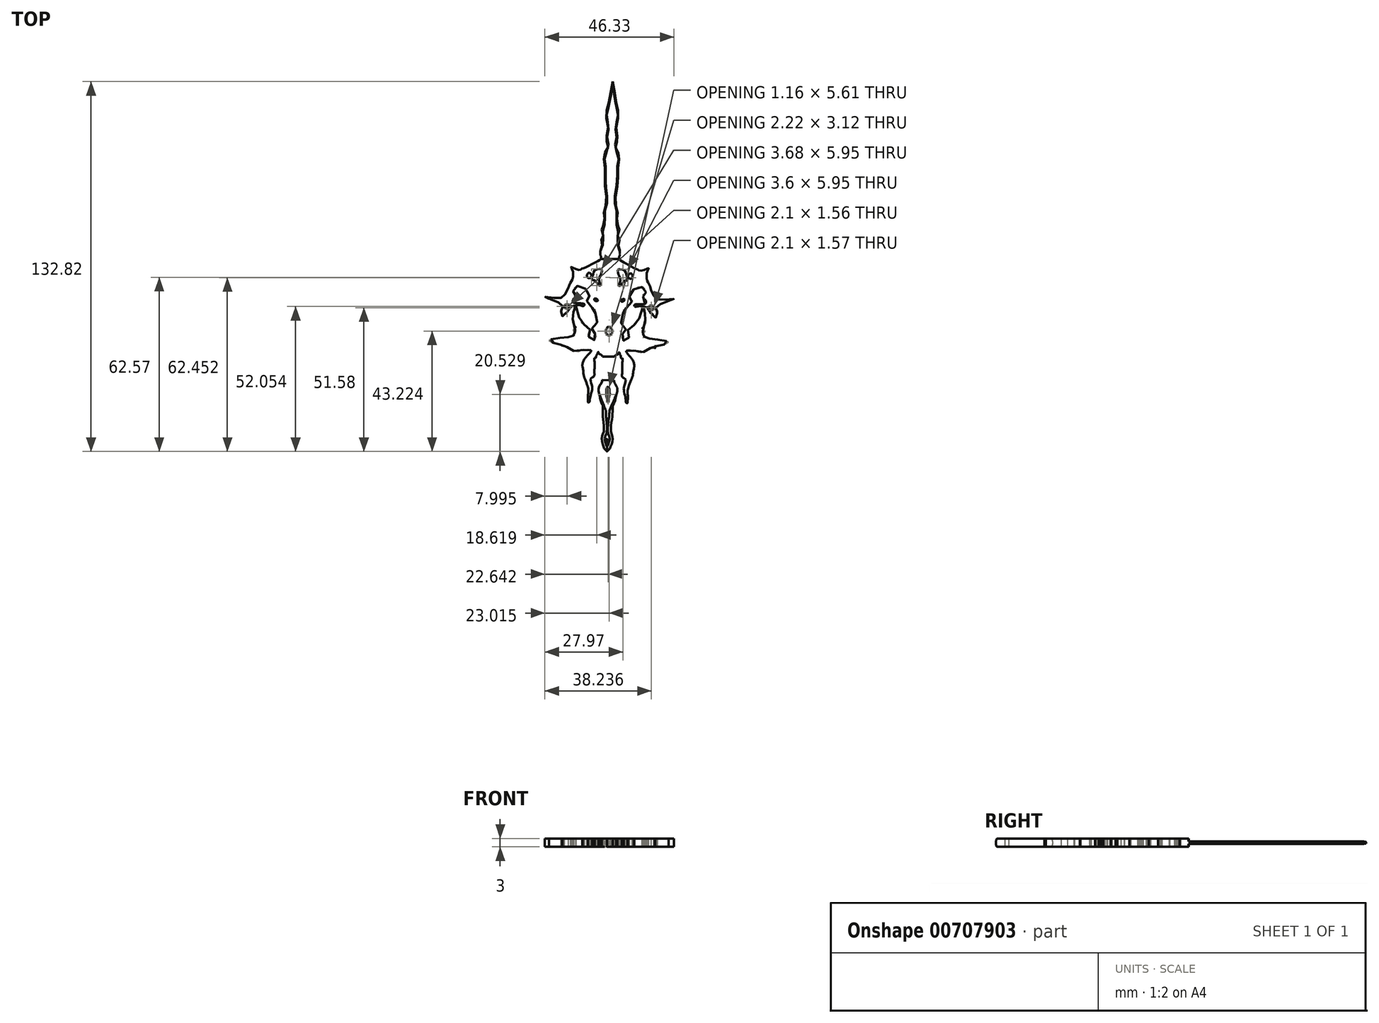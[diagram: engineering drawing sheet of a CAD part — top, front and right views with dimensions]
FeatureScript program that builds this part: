
annotation { "Feature Type Name" : "Feature", "Feature Type Description" : "" }
export const myFeature = defineFeature(function(context is Context, id is Id, definition is map)
    precondition{}
    {
        {
            var Q0;
            Q0=qCreatedBy(makeId("Top.planeOp"),FACE);
            var sketch = newSketch(context, id + "F0", { "sketchPlane" : qUnion([Q0])});
            skFitSpline(sketch, "E0", {"points": [v(17.67, 61.71) * mm, v(18.65, 55.7) * mm, v(19.3, 52.2) * mm, v(19.7, 49.3) * mm, v(18.9, 45.25) * mm, v(19.3, 41.85) * mm, v(19.22, 40.23) * mm, v(18.65, 38.77) * mm, v(19.14, 36.83) * mm, v(20.03, 35.45) * mm, v(19.7, 32.38) * mm, v(19.46, 28.25) * mm, v(19.3, 24.28) * mm, v(18.57, 19.18) * mm, v(19.14, 15.86) * mm, v(19.46, 13.6) * mm, v(19.06, 11.9) * mm, v(19.7, 9.47) * mm, v(20.1, 8.82) * mm, v(19.7, 7.77) * mm, v(19.54, 5.74) * mm, v(20.03, 4.85) * mm, v(19.79, 3.56) * mm, v(19.62, 2.42) * mm, v(20.2, 1.2) * mm], "startDerivative": vector(15.69, -96.68) * mm, "endDerivative": vector(24.07, -39.42) * mm});
            skFitSpline(sketch, "E1", {"points": [v(20.2, 1.2) * mm, v(20.2, 0.5) * mm, v(20.2, -0.63) * mm, v(19.94, -1.16) * mm, v(19.94, -2.05) * mm, v(20.7, -2.66) * mm, v(21.76, -3.3) * mm, v(23.21, -4.03) * mm, v(25.12, -5.2) * mm, v(26.5, -5.73) * mm, v(26.94, -6.06) * mm, v(28.64, -6.1) * mm, v(30.5, -5.29) * mm, v(29.93, -6.58) * mm, v(29.77, -8.24) * mm, v(29.97, -9.94) * mm, v(30.7, -11.03) * mm, v(31.3, -12.98) * mm], "startDerivative": vector(-0.52, -14.7) * mm, "endDerivative": vector(6.44, -29.47) * mm});
            skFitSpline(sketch, "E2", {"points": [v(31.3, -12.98) * mm, v(32.05, -14.07) * mm, v(32.4, -14.72) * mm, v(32.46, -15.57) * mm, v(32.94, -15.8) * mm, v(33.69, -16.22) * mm, v(33.93, -16.73) * mm, v(34.91, -16.7) * mm, v(36.55, -16.63) * mm, v(37.9, -16.49) * mm, v(39.61, -16.42) * mm, v(38.93, -16.9) * mm, v(37.84, -17.07) * mm, v(36.07, -17.65) * mm, v(34.88, -18.12) * mm, v(33.65, -18.77) * mm, v(33.28, -19.28) * mm, v(33.1, -19.48) * mm, v(33.21, -19.65) * mm, v(33.55, -19.86) * mm, v(33.76, -20.47) * mm, v(33.55, -21.6) * mm, v(33.48, -22.75) * mm, v(33.18, -23.26) * mm, v(32.87, -22.45) * mm, v(32.53, -21.9) * mm, v(31.3, -21.32) * mm, v(30.9, -20.88) * mm, v(30.05, -19.86) * mm, v(29.94, -19.04) * mm, v(28.62, -18.87) * mm, v(26.95, -18.9) * mm, v(25.62, -19.11) * mm, v(25.35, -18.57) * mm, v(27.19, -18.23) * mm, v(29.5, -17.88) * mm, v(29.23, -16.6) * mm, v(28.51, -15.16) * mm, v(28.65, -14.55) * mm, v(29.23, -14.45) * mm, v(29.6, -13.6) * mm, v(29.13, -12.64) * mm, v(28.1, -12.03) * mm, v(26.75, -12.13) * mm, v(25.11, -12.98) * mm, v(24.43, -13.83) * mm, v(23.65, -15.4) * mm, v(23.85, -16.32) * mm, v(24.6, -16.83) * mm, v(24.16, -17.75) * mm, v(23.17, -18.97) * mm, v(22.15, -19.86) * mm, v(21.54, -20.13) * mm, v(21.3, -21.42) * mm, v(20.86, -22.62) * mm, v(20.62, -24.73) * mm, v(20.82, -25.2) * mm], "startDerivative": vector(39.41, -59.59) * mm, "endDerivative": vector(20, -28.18) * mm});
            skFitSpline(sketch, "E3", {"points": [v(20.82, -25.2) * mm, v(21.39, -25.9) * mm, v(21.96, -26.55) * mm, v(22.4, -27.3) * mm, v(22.48, -27.93) * mm, v(21.9, -28.38) * mm, v(21.25, -28.93) * mm, v(20.82, -29.79) * mm, v(21.1, -30.82) * mm, v(21.5, -31.3) * mm, v(22.42, -31.19) * mm, v(23.25, -30.7) * mm, v(23.5, -29.82) * mm, v(23.65, -28.64) * mm, v(23.2, -27.9) * mm, v(23.14, -27.13) * mm, v(24.34, -26.35) * mm, v(25.4, -25.67) * mm, v(26.23, -25.2) * mm, v(26.94, -23.72) * mm, v(27.83, -21.57) * mm, v(28.49, -19.17) * mm, v(29.03, -19.28) * mm, v(29.17, -20.28) * mm, v(29.23, -21.97) * mm, v(29.06, -23.5) * mm, v(29.03, -23.86) * mm, v(29.63, -24.12) * mm, v(29.4, -25.2) * mm, v(28.92, -26.15) * mm, v(28.32, -26.75) * mm, v(28.23, -27.7) * mm, v(28.26, -28.24) * mm, v(28.8, -27.81) * mm, v(29.17, -27.87) * mm, v(28.95, -28.44) * mm, v(28.49, -29.07) * mm, v(28.23, -29.67) * mm, v(28.29, -30.27) * mm, v(28.86, -29.99) * mm, v(29.38, -29.93) * mm, v(29.66, -30.16) * mm, v(30.23, -30.45) * mm, v(30.86, -30.5) * mm, v(31.98, -30.7) * mm, v(33.24, -30.82) * mm, v(34.36, -30.99) * mm, v(35.7, -31.19) * mm, v(37.16, -31.53) * mm, v(37.65, -31.8) * mm, v(36.87, -32.5) * mm, v(35.36, -32.7) * mm, v(33.87, -32.8) * mm, v(33.73, -33.25) * mm, v(32.78, -33.28) * mm, v(32.8, -34.02) * mm, v(30.52, -34.05) * mm, v(30.1, -34.57) * mm, v(29, -35.17) * mm, v(27.6, -35.63) * mm, v(25.51, -35.02) * mm, v(24.14, -34.68) * mm, v(22.9, -34.68) * mm, v(22.42, -35) * mm, v(23.14, -36.23) * mm, v(24.4, -37.69) * mm, v(25.23, -39.46) * mm, v(25.37, -40.75) * mm, v(25.28, -40.92) * mm], "startDerivative": vector(39.82, -50.4) * mm, "endDerivative": vector(-15.61, -19.42) * mm});
            skFitSpline(sketch, "E4", {"points": [v(25.28, -41.1) * mm, v(25.1, -41.81) * mm, v(24.99, -42.89) * mm, v(24.7, -44.22) * mm, v(24.16, -45.74) * mm, v(23.39, -47.66) * mm, v(23.06, -48.68) * mm, v(22.96, -50.17) * mm, v(23.06, -51.71) * mm, v(22.96, -53.3) * mm], "startDerivative": vector(-2.44, -8.3) * mm, "endDerivative": vector(-1.39, -13.44) * mm});
            skFitSpline(sketch, "E5", {"points": [v(25.28, -40.92) * mm, v(25.28, -41.1) * mm, v(25.27, -41.1) * mm], "startDerivative": vector(0.03, -0.33) * mm, "endDerivative": vector(-0.07, 0.03) * mm});
            skFitSpline(sketch, "E6", {"points": [v(22.96, -53.3) * mm, v(22.96, -53.67) * mm, v(22.57, -53.72) * mm, v(22.4, -53.3) * mm, v(22.3, -52.36) * mm, v(22.13, -51.39) * mm, v(21.79, -49.92) * mm, v(21.62, -48.61) * mm, v(21.77, -47.6) * mm, v(22.25, -45.9) * mm, v(22.11, -44.97) * mm, v(21.26, -44.55) * mm, v(20.9, -43.54) * mm, v(21, -43.17) * mm], "startDerivative": vector(2.26, -8.44) * mm, "endDerivative": vector(2.8, 5.94) * mm});
            skFitSpline(sketch, "E7", {"points": [v(21, -43.17) * mm, v(21, -42.56) * mm, v(21, -41.73) * mm, v(21, -40.73) * mm, v(21, -39.6) * mm, v(21.2, -38.25) * mm, v(21.17, -37.74) * mm, v(20.7, -37.66) * mm, v(20.53, -36.89) * mm, v(20.16, -36.12) * mm, v(19.9, -35.41) * mm, v(19.64, -36.04) * mm, v(18.79, -36.46) * mm, v(18.28, -37.1) * mm, v(18.46, -37.96) * mm, v(18.56, -38.73) * mm, v(18.22, -39.28) * mm, v(17.85, -39.88) * mm, v(18.18, -40.76) * mm, v(18.28, -42.13) * mm, v(18.18, -44) * mm, v(18.18, -45.53) * mm, v(18.24, -46.28) * mm, v(18.83, -47.35) * mm, v(19.25, -48.32) * mm, v(19.21, -49.82) * mm, v(18.85, -50.87) * mm], "startDerivative": vector(0.02, 19.02) * mm, "endDerivative": vector(-9.98, -23.15) * mm});
            skFitSpline(sketch, "E8", {"points": [v(18.85, -50.87) * mm, v(18.34, -53.3) * mm, v(17.69, -54.56) * mm, v(17.57, -56.3) * mm, v(17.45, -58.53) * mm, v(17.08, -61.32) * mm, v(17.04, -64.28) * mm, v(17.65, -66.22) * mm, v(17.16, -68.65) * mm, v(16.52, -70.1) * mm, v(15.58, -71.1) * mm], "startDerivative": vector(-3.2, -24.62) * mm, "endDerivative": vector(-12.6, -11.64) * mm});
            skFitSpline(sketch, "E9.MirrorCS", {"points": [v(17.67, 61.71) * mm, v(16.5, 55.72) * mm, v(15.74, 52.27) * mm, v(15.25, 49.37) * mm, v(15.93, 45.3) * mm, v(15.42, 41.9) * mm, v(15.45, 40.29) * mm, v(15.97, 38.81) * mm, v(15.42, 36.89) * mm, v(14.49, 35.54) * mm, v(14.71, 32.45) * mm, v(14.83, 28.32) * mm, v(14.86, 24.35) * mm, v(15.43, 19.23) * mm, v(14.76, 15.93) * mm, v(14.37, 13.67) * mm, v(14.72, 11.96) * mm, v(14, 9.56) * mm, v(13.57, 8.92) * mm, v(13.94, 7.86) * mm, v(14.04, 5.83) * mm, v(13.52, 4.95) * mm, v(13.73, 3.65) * mm, v(13.85, 2.51) * mm, v(13.25, 1.32) * mm], "startDerivative": vector(-18.72, -96.13) * mm, "endDerivative": vector(-25.3, -38.64) * mm});
            skFitSpline(sketch, "E10.MirrorCS", {"points": [v(13.25, 1.32) * mm, v(13.22, 0.61) * mm, v(13.19, -0.52) * mm, v(13.42, -1.06) * mm, v(13.4, -1.95) * mm, v(12.61, -2.53) * mm, v(11.54, -3.14) * mm, v(10.06, -3.82) * mm, v(8.12, -4.94) * mm, v(6.73, -5.42) * mm, v(6.27, -5.73) * mm, v(4.57, -5.72) * mm, v(2.74, -4.85) * mm, v(3.26, -6.16) * mm, v(3.37, -7.83) * mm, v(3.12, -9.52) * mm, v(2.36, -10.59) * mm, v(1.69, -12.51) * mm], "startDerivative": vector(0.06, -14.7) * mm, "endDerivative": vector(-7.36, -29.25) * mm});
            skFitSpline(sketch, "E11.MirrorCS", {"points": [v(1.69, -12.51) * mm, v(0.9, -13.58) * mm, v(0.55, -14.22) * mm, v(0.45, -15.07) * mm, v(-0.03, -15.29) * mm, v(-0.8, -15.67) * mm, v(-1.05, -16.18) * mm, v(-2.03, -16.11) * mm, v(-3.66, -16) * mm, v(-5.02, -15.81) * mm, v(-6.72, -15.7) * mm, v(-6.05, -16.19) * mm, v(-4.97, -16.4) * mm, v(-3.22, -17.03) * mm, v(-2.04, -17.54) * mm, v(-0.84, -18.23) * mm, v(-0.48, -18.75) * mm, v(-0.32, -18.96) * mm, v(-0.42, -19.12) * mm, v(-0.77, -19.32) * mm, v(-1, -19.92) * mm, v(-0.83, -21.05) * mm, v(-0.8, -22.21) * mm, v(-0.5, -22.73) * mm, v(-0.17, -21.93) * mm, v(0.18, -21.4) * mm, v(1.42, -20.85) * mm, v(1.85, -20.42) * mm, v(2.73, -19.43) * mm, v(2.86, -18.62) * mm, v(4.2, -18.49) * mm, v(5.86, -18.57) * mm, v(7.18, -18.82) * mm, v(7.47, -18.28) * mm, v(5.64, -17.89) * mm, v(3.34, -17.47) * mm, v(3.65, -16.19) * mm, v(4.41, -14.78) * mm, v(4.3, -14.17) * mm, v(3.72, -14.05) * mm, v(3.37, -13.18) * mm, v(3.88, -12.25) * mm, v(4.92, -11.67) * mm, v(6.28, -11.81) * mm, v(7.88, -12.7) * mm, v(8.54, -13.58) * mm, v(9.27, -15.17) * mm, v(9.04, -16.09) * mm, v(8.27, -16.57) * mm, v(8.68, -17.5) * mm, v(9.63, -18.76) * mm, v(10.63, -19.68) * mm, v(11.23, -19.97) * mm, v(11.43, -21.27) * mm, v(11.83, -22.47) * mm, v(12, -24.6) * mm, v(11.78, -25.06) * mm], "startDerivative": vector(-41.27, -58.32) * mm, "endDerivative": vector(-20.87, -27.53) * mm});
            skFitSpline(sketch, "E12.MirrorCS", {"points": [v(11.78, -25.06) * mm, v(11.2, -25.73) * mm, v(10.6, -26.37) * mm, v(10.15, -27.1) * mm, v(10.04, -27.73) * mm, v(10.6, -28.2) * mm, v(11.24, -28.77) * mm, v(11.64, -29.64) * mm, v(11.33, -30.66) * mm, v(10.91, -31.14) * mm, v(10, -31) * mm, v(9.18, -30.48) * mm, v(8.95, -29.59) * mm, v(8.85, -28.4) * mm, v(9.33, -27.68) * mm, v(9.41, -26.9) * mm, v(8.23, -26.1) * mm, v(7.2, -25.38) * mm, v(6.38, -24.9) * mm, v(5.71, -23.38) * mm, v(4.9, -21.21) * mm, v(4.31, -18.79) * mm, v(3.77, -18.88) * mm, v(3.6, -19.88) * mm, v(3.48, -21.57) * mm, v(3.6, -23.09) * mm, v(3.62, -23.46) * mm, v(3.01, -23.7) * mm, v(3.2, -24.8) * mm, v(3.66, -25.75) * mm, v(4.25, -26.37) * mm, v(4.3, -27.32) * mm, v(4.26, -27.86) * mm, v(3.73, -27.42) * mm, v(3.35, -27.46) * mm, v(3.56, -28.04) * mm, v(4, -28.69) * mm, v(4.24, -29.3) * mm, v(4.16, -29.9) * mm, v(3.6, -29.59) * mm, v(3.09, -29.52) * mm, v(2.8, -29.74) * mm, v(2.21, -30) * mm, v(1.58, -30.04) * mm, v(0.46, -30.2) * mm, v(-0.8, -30.28) * mm, v(-1.92, -30.42) * mm, v(-3.28, -30.58) * mm, v(-4.75, -30.87) * mm, v(-5.24, -31.12) * mm, v(-4.49, -31.85) * mm, v(-2.98, -32.1) * mm, v(-1.5, -32.24) * mm, v(-1.37, -32.7) * mm, v(-0.42, -32.76) * mm, v(-0.48, -33.5) * mm, v(1.81, -33.6) * mm, v(2.23, -34.13) * mm, v(3.3, -34.76) * mm, v(4.68, -35.26) * mm, v(6.79, -34.73) * mm, v(8.17, -34.43) * mm, v(9.4, -34.47) * mm, v(9.88, -34.8) * mm, v(9.12, -36) * mm, v(7.82, -37.43) * mm, v(6.93, -39.17) * mm, v(6.75, -40.46) * mm, v(6.83, -40.63) * mm], "startDerivative": vector(-41.39, -49.11) * mm, "endDerivative": vector(15, -19.9) * mm});
            skFitSpline(sketch, "E13.MirrorCS", {"points": [v(11.78, -25.06) * mm, v(11.2, -25.73) * mm, v(10.6, -26.37) * mm, v(10.15, -27.1) * mm, v(10.04, -27.73) * mm, v(10.6, -28.2) * mm, v(11.24, -28.77) * mm, v(11.64, -29.64) * mm, v(11.33, -30.66) * mm, v(10.91, -31.14) * mm, v(10, -31) * mm, v(9.18, -30.48) * mm, v(8.95, -29.59) * mm, v(8.85, -28.4) * mm, v(9.33, -27.68) * mm, v(9.41, -26.9) * mm, v(8.23, -26.1) * mm, v(7.2, -25.38) * mm, v(6.38, -24.9) * mm, v(5.71, -23.38) * mm, v(4.9, -21.21) * mm, v(4.31, -18.79) * mm, v(3.77, -18.88) * mm, v(3.6, -19.88) * mm, v(3.48, -21.57) * mm, v(3.6, -23.09) * mm, v(3.62, -23.46) * mm, v(3.01, -23.7) * mm, v(3.2, -24.8) * mm, v(3.66, -25.75) * mm, v(4.25, -26.37) * mm, v(4.3, -27.32) * mm, v(4.26, -27.86) * mm, v(3.73, -27.42) * mm, v(3.35, -27.46) * mm, v(3.56, -28.04) * mm, v(4, -28.69) * mm, v(4.24, -29.3) * mm, v(4.16, -29.9) * mm, v(3.6, -29.59) * mm, v(3.09, -29.52) * mm, v(2.8, -29.74) * mm, v(2.21, -30) * mm, v(1.58, -30.04) * mm, v(0.46, -30.2) * mm, v(-0.8, -30.28) * mm, v(-1.92, -30.42) * mm, v(-3.28, -30.58) * mm, v(-4.75, -30.87) * mm, v(-5.24, -31.12) * mm, v(-4.49, -31.85) * mm, v(-2.98, -32.1) * mm, v(-1.5, -32.24) * mm, v(-1.37, -32.7) * mm, v(-0.42, -32.76) * mm, v(-0.48, -33.5) * mm, v(1.81, -33.6) * mm, v(2.23, -34.13) * mm, v(3.3, -34.76) * mm, v(4.68, -35.26) * mm, v(6.79, -34.73) * mm, v(8.17, -34.43) * mm, v(9.4, -34.47) * mm, v(9.88, -34.8) * mm, v(9.12, -36) * mm, v(7.82, -37.43) * mm, v(6.93, -39.17) * mm, v(6.75, -40.46) * mm, v(6.83, -40.63) * mm], "startDerivative": vector(-41.39, -49.11) * mm, "endDerivative": vector(15, -19.9) * mm});
            skFitSpline(sketch, "E14.MirrorCS", {"points": [v(11.04, -43.01) * mm, v(11.06, -42.4) * mm, v(11.08, -41.57) * mm, v(11.11, -40.58) * mm, v(11.15, -39.45) * mm, v(11, -38.09) * mm, v(11.04, -37.58) * mm, v(11.5, -37.51) * mm, v(11.71, -36.75) * mm, v(12.1, -36) * mm, v(12.39, -35.3) * mm, v(12.63, -35.93) * mm, v(13.47, -36.38) * mm, v(13.95, -37.02) * mm, v(13.74, -37.89) * mm, v(13.62, -38.65) * mm, v(13.94, -39.21) * mm, v(14.29, -39.83) * mm, v(13.94, -40.69) * mm, v(13.8, -42.06) * mm, v(13.84, -43.92) * mm, v(13.79, -45.46) * mm, v(13.7, -46.2) * mm, v(13.08, -47.26) * mm, v(12.63, -48.22) * mm, v(12.62, -49.72) * mm, v(12.95, -50.78) * mm], "startDerivative": vector(0.58, 19.02) * mm, "endDerivative": vector(9.24, -23.45) * mm});
            skFitSpline(sketch, "E15.MirrorCS", {"points": [v(12.95, -50.78) * mm, v(13.38, -53.23) * mm, v(14, -54.5) * mm, v(14.06, -56.25) * mm, v(14.1, -58.48) * mm, v(14.38, -61.28) * mm, v(14.33, -64.24) * mm, v(13.66, -66.16) * mm, v(14.07, -68.6) * mm, v(14.67, -70.08) * mm, v(15.58, -71.1) * mm], "startDerivative": vector(2.42, -24.71) * mm, "endDerivative": vector(12.24, -12.03) * mm});
            skFitSpline(sketch, "E16.MirrorCS", {"points": [v(8.76, -53.09) * mm, v(8.75, -53.44) * mm, v(9.14, -53.5) * mm, v(9.32, -53.1) * mm, v(9.45, -52.16) * mm, v(9.66, -51.2) * mm, v(10.04, -49.74) * mm, v(10.25, -48.43) * mm, v(10.13, -47.43) * mm, v(9.7, -45.71) * mm, v(9.87, -44.78) * mm, v(10.74, -44.38) * mm, v(11.13, -43.39) * mm, v(11.04, -43.01) * mm], "startDerivative": vector(-2.52, -8.36) * mm, "endDerivative": vector(-2.61, 6.03) * mm});
            skFitSpline(sketch, "E17.MirrorCS", {"points": [v(6.83, -40.82) * mm, v(6.98, -41.53) * mm, v(7.07, -42.6) * mm, v(7.3, -43.95) * mm, v(7.8, -45.48) * mm, v(8.51, -47.43) * mm, v(8.8, -48.45) * mm, v(8.86, -49.95) * mm, v(8.7, -51.48) * mm, v(8.76, -53.09) * mm], "startDerivative": vector(2.18, -8.36) * mm, "endDerivative": vector(0.97, -13.47) * mm});
            skFitSpline(sketch, "E18", {"points": [v(15.95, -47.78) * mm, v(15.48, -48.38) * mm, v(15.33, -49.92) * mm, v(15.48, -51.7) * mm, v(15.86, -53.02) * mm, v(15.86, -53.5) * mm, v(16.22, -51.75) * mm, v(16.56, -50.18) * mm, v(16.2, -48.04) * mm, v(15.95, -47.78) * mm]});
            skEllipse(sketch, "E19", {"center": v(16.3, -27.89) * mm, "majorRadius": 1.56 * mm, "minorRadius": 1.1 * mm, "majorAxis": v(0, 1)});
            skFitSpline(sketch, "E20", {"points": [v(30.6, -19) * mm, v(32.47, -19.05) * mm, v(32.07, -20.17) * mm, v(30.72, -20) * mm, v(30.6, -19) * mm]});
            skFitSpline(sketch, "E21.MirrorC", {"points": [v(2.2, -18.55) * mm, v(0.34, -18.55) * mm, v(0.7, -19.67) * mm, v(2.05, -19.54) * mm, v(2.2, -18.55) * mm]});
            skFitSpline(sketch, "E22", {"points": [v(21.35, -16.34) * mm, v(21.9, -16.5) * mm, v(21.21, -17.3) * mm, v(20.53, -16.98) * mm, v(21.35, -16.34) * mm]});
            skFitSpline(sketch, "E23.MirrorC", {"points": [v(11.54, -16.18) * mm, v(10.99, -16.34) * mm, v(11.64, -17.14) * mm, v(12.33, -16.85) * mm, v(11.54, -16.18) * mm]});
            skFitSpline(sketch, "E24", {"points": [v(20.33, -5.68) * mm, v(22.13, -6.36) * mm, v(22.6, -7.93) * mm, v(23.05, -9.6) * mm, v(22.2, -9.77) * mm, v(21.1, -10.58) * mm, v(20.2, -11.7) * mm, v(19.85, -11.64) * mm, v(20.16, -10.41) * mm, v(20.4, -9.26) * mm, v(19.99, -8.2) * mm, v(19.48, -6.8) * mm, v(19.5, -5.85) * mm, v(20.33, -5.68) * mm]});
            skFitSpline(sketch, "E25.MirrorC", {"points": [v(12.9, -5.57) * mm, v(11.07, -6.19) * mm, v(10.54, -7.74) * mm, v(10.05, -9.4) * mm, v(10.9, -9.59) * mm, v(11.96, -10.44) * mm, v(12.84, -11.6) * mm, v(13.18, -11.53) * mm, v(12.92, -10.3) * mm, v(12.71, -9.14) * mm, v(13.15, -8.1) * mm, v(13.7, -6.72) * mm, v(13.7, -5.76) * mm, v(12.9, -5.57) * mm]});
            skFitSpline(sketch, "E26", {"points": [v(24.04, -7.15) * mm, v(24.79, -8.1) * mm, v(24.24, -9.05) * mm, v(23.22, -8.61) * mm, v(23.29, -7.73) * mm, v(24.04, -7.15) * mm]});
            skFitSpline(sketch, "E27.MirrorC", {"points": [v(9.14, -6.91) * mm, v(8.36, -7.84) * mm, v(8.88, -8.81) * mm, v(9.91, -8.4) * mm, v(9.87, -7.51) * mm, v(9.14, -6.91) * mm]});
            skFitSpline(sketch, "E28", {"points": [v(15.65, -66.7) * mm, v(15.23, -66.8) * mm, v(15.16, -67.95) * mm, v(15.94, -67.68) * mm, v(15.65, -66.7) * mm]});
            skLineSegment(sketch, "E29", {"start": v(13.4, -1.95) * mm, "end": v(19.94, -2.05) * mm});
            skLineSegment(sketch, "E30", {"start": v(12, -24.6) * mm, "end": v(20.62, -24.73) * mm});
            skLineSegment(sketch, "E31", {"start": v(13.79, -45.46) * mm, "end": v(18.18, -45.53) * mm});
            skLineSegment(sketch, "E32", {"start": v(9.88, -34.8) * mm, "end": v(22.42, -35) * mm});
            skLineSegment(sketch, "E33", {"start": v(6.83, -40.82) * mm, "end": v(6.83, -40.63) * mm});
            skLineSegment(sketch, "E34", {"start": v(18.28, -37.1) * mm, "end": v(13.95, -37.02) * mm});
            skSolve(sketch);
        }
        {
            var Q0;
            {var subQ4=sQuery(id+"F0.wireOp",EDGE,"E0");Q0=makeQuery(id+"F0.imprint","IMPRINT",FACE,{"disambiguationData":[TD([[makeQuery(id+"F0.imprint","IMPRINT",EDGE,{"derivedFrom":subQ4}),-1.0]])]});}
            extrude(context, id + "F1", {"entities" : qUnion([Q0]), "endBound" : BoundingType.SYMMETRIC, "depth" : 1 * mm, "offsetDistance" : 25 * mm});
        }
        {
            var Q0;
            Q0=makeQuery(id+"F0.imprint","IMPRINT",FACE,{"disambiguationData":[TD([[makeQuery(id+"F0.imprint","IMPRINT",EDGE,{"derivedFrom":sQuery(id+"F0.wireOp",EDGE,"E20")}),1.0]])]});
            var Q1;
            Q1=makeQuery(id+"F0.imprint","IMPRINT",FACE,{"disambiguationData":[TD([[makeQuery(id+"F0.imprint","IMPRINT",EDGE,{"derivedFrom":sQuery(id+"F0.wireOp",EDGE,"E19")}),-1.0]])]});
            var Q2;
            Q2=makeQuery(id+"F0.imprint","IMPRINT",FACE,{"disambiguationData":[TD([[makeQuery(id+"F0.imprint","IMPRINT",EDGE,{"derivedFrom":sQuery(id+"F0.wireOp",EDGE,"E4")}),-1.0]])]});
            var Q3;
            {var subQ1=sQuery(id+"F0.wireOp",EDGE,"E8");Q3=makeQuery(id+"F0.imprint","IMPRINT",FACE,{"disambiguationData":[TD([[makeQuery(id+"F0.imprint","IMPRINT",EDGE,{"derivedFrom":subQ1}),-1.0]])]});}
            extrude(context, id + "F2", {"entities" : qUnion([Q0, Q1, Q2, Q3]), "operationType" : NewBodyOperationType.ADD, "endBound" : BoundingType.SYMMETRIC, "depth" : 3 * mm, "offsetDistance" : 25 * mm});
        }
        {
            var Q0;
            Q0=makeQuery(id+"F1.opExtrude","CAP_EDGE",EDGE,{"disambiguationData":[OSD([sQuery(id+"F0.wireOp",EDGE,"E0")])],"isStart":false});
            var Q1;
            Q1=makeQuery(id+"F1.opExtrude","CAP_EDGE",EDGE,{"disambiguationData":[OSD([sQuery(id+"F0.wireOp",EDGE,"E9.MirrorCS")])],"isStart":false});
            chamfer(context, id + "F3", {"entities" : qUnion([Q0, Q1]), "chamferType" : ChamferType.OFFSET_ANGLE, "width" : 0.25 * mm, "oppositeDirection" : false, "angle" : 45 * degree, "tangentPropagation" : true});
        }
        {
            var Q0;
            Q0=makeQuery(id+"F1.opExtrude","CAP_EDGE",EDGE,{"disambiguationData":[OSD([sQuery(id+"F0.wireOp",EDGE,"E9.MirrorCS")])],"isStart":true});
            var Q1;
            Q1=makeQuery(id+"F1.opExtrude","CAP_EDGE",EDGE,{"disambiguationData":[OSD([sQuery(id+"F0.wireOp",EDGE,"E0")])],"isStart":true});
            chamfer(context, id + "F4", {"entities" : qUnion([Q0, Q1]), "chamferType" : ChamferType.OFFSET_ANGLE, "width" : 0.25 * mm, "oppositeDirection" : false, "angle" : 45 * degree, "tangentPropagation" : true});
        }
        {
            var Q0;
            Q0=makeQuery(id+"F2.opExtrude","CAP_EDGE",EDGE,{"disambiguationData":[OSD([sQuery(id+"F0.wireOp",EDGE,"E15.MirrorCS")])],"isStart":true});
            var Q1;
            Q1=makeQuery(id+"F2.opExtrude","CAP_EDGE",EDGE,{"disambiguationData":[OSD([sQuery(id+"F0.wireOp",EDGE,"E8")])],"isStart":true});
            var Q2;
            Q2=makeQuery(id+"F2.opExtrude","CAP_EDGE",EDGE,{"disambiguationData":[OSD([sQuery(id+"F0.wireOp",EDGE,"E15.MirrorCS")])],"isStart":false});
            var Q3;
            Q3=makeQuery(id+"F2.opExtrude","CAP_EDGE",EDGE,{"disambiguationData":[OSD([sQuery(id+"F0.wireOp",EDGE,"E8")])],"isStart":false});
            fillet(context, id + "F5", {"entities" : qUnion([Q0, Q1, Q2, Q3]), "radius" : 1.11 * mm, "tangentPropagation" : true, "rho" : 0.71, "crossSection" : FilletCrossSection.CONIC, "allowEdgeOverflow" : false});
        }
    });
